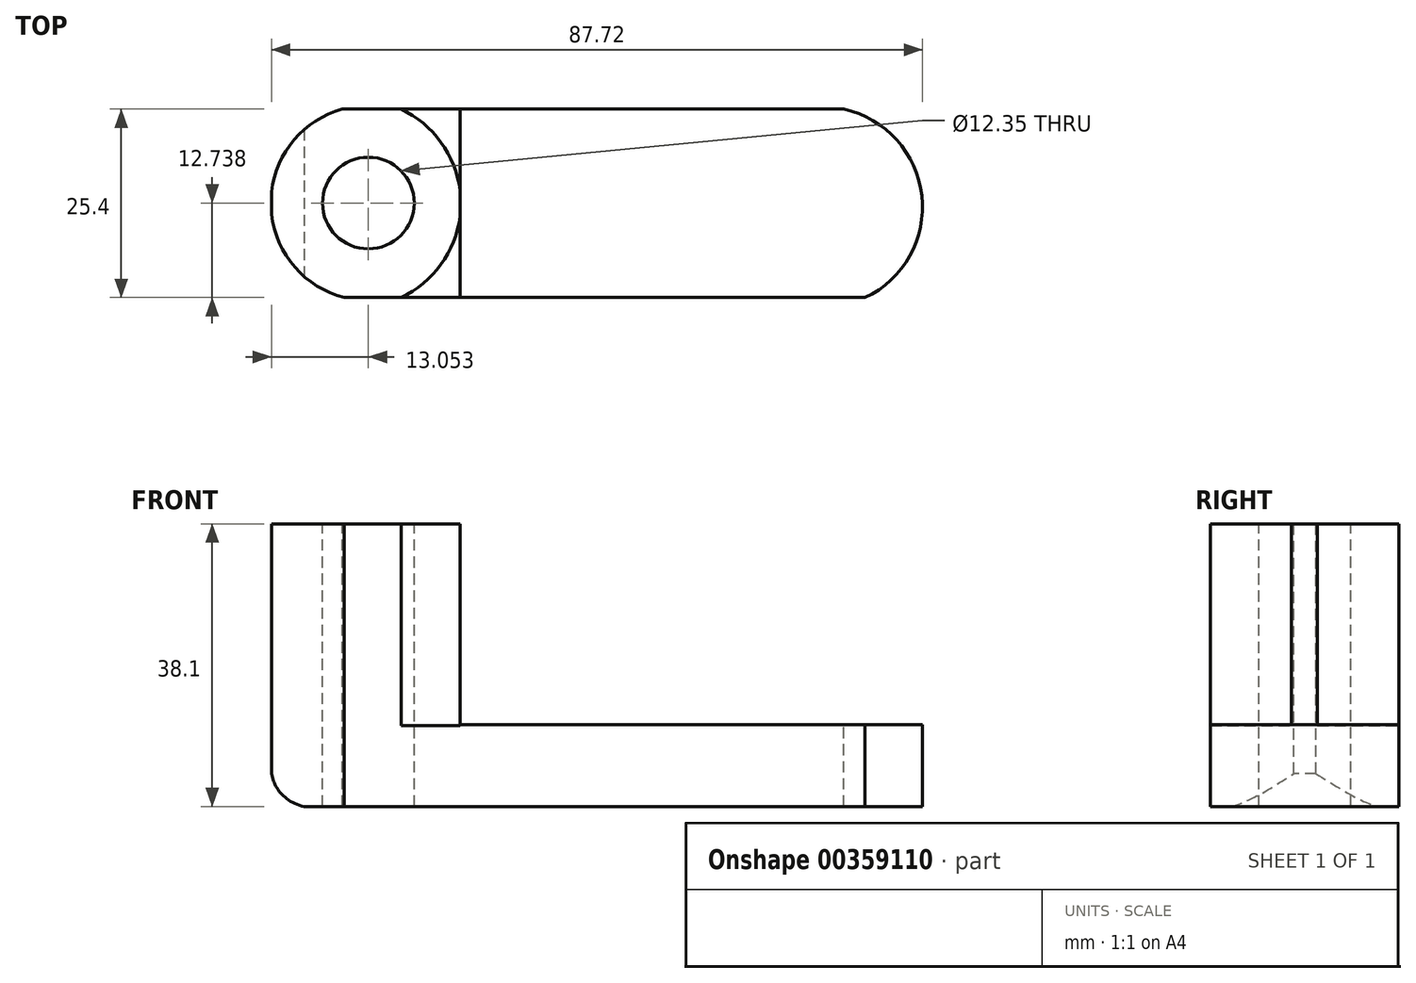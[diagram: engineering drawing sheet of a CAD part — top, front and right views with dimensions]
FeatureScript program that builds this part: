
annotation { "Feature Type Name" : "Feature", "Feature Type Description" : "" }
export const myFeature = defineFeature(function(context is Context, id is Id, definition is map)
    precondition{}
    {
        {
            var Q0;
            Q0=qCreatedBy(makeId("Front.planeOp"),FACE);
            var sketch = newSketch(context, id + "F0", { "sketchPlane" : qUnion([Q0])});
            skLineSegment(sketch, "E0", {"start": v(-42.33, 0) * mm, "end": v(-42.33, 38.1) * mm});
            skLineSegment(sketch, "E1", {"start": v(-42.33, 38.1) * mm, "end": v(-16.93, 38.1) * mm});
            skLineSegment(sketch, "E2", {"start": v(-16.93, 38.1) * mm, "end": v(-16.93, 11) * mm});
            skLineSegment(sketch, "E3", {"start": v(-16.93, 11) * mm, "end": v(46.57, 11) * mm});
            skLineSegment(sketch, "E4", {"start": v(46.57, 11) * mm, "end": v(46.57, 0) * mm});
            skLineSegment(sketch, "E5", {"start": v(46.57, 0) * mm, "end": v(-42.33, 0) * mm});
            skSolve(sketch);
        }
        {
            var Q0;
            Q0=makeQuery(id+"F0.imprint","IMPRINT",FACE,{"disambiguationData":[TD([[makeQuery(id+"F0.imprint","IMPRINT",EDGE,{"derivedFrom":sQuery(id+"F0.wireOp",EDGE,"E0")}),-1.0]])]});
            extrude(context, id + "F1", {"entities" : qUnion([Q0]), "depth" : 25.4 * mm});
        }
        {
            var Q0;
            Q0=makeQuery(id+"F1.opExtrude","CAP_FACE",FACE,{"disambiguationData":[OSD([sQuery(id+"F0.wireOp",EDGE,"E0"),sQuery(id+"F0.wireOp",EDGE,"E1"),sQuery(id+"F0.wireOp",EDGE,"E2"),sQuery(id+"F0.wireOp",EDGE,"E3"),sQuery(id+"F0.wireOp",EDGE,"E4"),sQuery(id+"F0.wireOp",EDGE,"E5")])],"isStart":false});
            var sketch = newSketch(context, id + "F2", { "sketchPlane" : qUnion([Q0])});
            skArc(sketch, "E6", {"start": v(-42.33, 4.42) * mm, "mid": v(-40.05, 0.89) * mm, "end": v(-35.94, 0) * mm});
            skSolve(sketch);
        }
        {
            var Q0;
            {var subQ0=sQuery(id+"F2.wireOp",EDGE,"E6");var subQ1=makeQuery(id+"F1.opExtrude","CAP_EDGE",EDGE,{"disambiguationData":[OSD([sQuery(id+"F0.wireOp",EDGE,"E0")])],"isStart":false});var subQ2=makeQuery(id+"F2.imprint","INTERSECT",VERTEX,{"derivedFrom":[subQ1,subQ0]});Q0=makeQuery(id+"F2.imprint","IMPRINT",FACE,{"disambiguationData":[TD([[makeQuery(id+"F2.imprint","IMPRINT",EDGE,{"disambiguationData":[TD([[subQ2,-1.0]])],"derivedFrom":subQ0}),-1.0]])]});}
            extrude(context, id + "F3", {"entities" : qUnion([Q0]), "operationType" : NewBodyOperationType.REMOVE, "oppositeDirection" : true, "depth" : 25.4 * mm});
        }
        {
            var Q0;
            Q0=makeQuery(id+"F1.opExtrude","SWEPT_FACE",FACE,{"disambiguationData":[OSD([sQuery(id+"F0.wireOp",EDGE,"E3")])]});
            var sketch = newSketch(context, id + "F4", { "sketchPlane" : qUnion([Q0])});
            skArc(sketch, "E7", {"start": v(37.65, -25.4) * mm, "mid": v(45.3, -11.68) * mm, "end": v(34.8, 0) * mm});
            skSolve(sketch);
        }
        {
            var Q0;
            {var subQ0=sQuery(id+"F4.wireOp",EDGE,"E7");Q0=makeQuery(id+"F4.imprint","IMPRINT",FACE,{"disambiguationData":[TD([[makeQuery(id+"F4.imprint","IMPRINT",EDGE,{"derivedFrom":subQ0}),-1.0]])]});}
            extrude(context, id + "F5", {"entities" : qUnion([Q0]), "operationType" : NewBodyOperationType.REMOVE, "oppositeDirection" : true, "depth" : 25.4 * mm});
        }
        {
            var Q0;
            Q0=makeQuery(id+"F1.opExtrude","SWEPT_FACE",FACE,{"disambiguationData":[OSD([sQuery(id+"F0.wireOp",EDGE,"E1")])]});
            var sketch = newSketch(context, id + "F6", { "sketchPlane" : qUnion([Q0])});
            skCircle(sketch, "E8", {"center": v(-31.1, -11.27) * mm, "radius": 19.57 * mm});
            skSolve(sketch);
        }
        {
            var Q0;
            {var subQ0=sQuery(id+"F0.wireOp",EDGE,"E1");var subQ1=makeQuery(id+"F1.opExtrude","CAP_EDGE",EDGE,{"disambiguationData":[OSD([subQ0])],"isStart":true});Q0=makeQuery(id+"F6.imprint","IMPRINT",FACE,{"disambiguationData":[TD([[makeQuery(id+"F6.imprint","IMPRINT",EDGE,{"derivedFrom":subQ1}),1.0]])]});}
            extrude(context, id + "F7", {"entities" : qUnion([Q0]), "operationType" : NewBodyOperationType.REMOVE, "oppositeDirection" : true, "depth" : 25.4 * mm});
        }
        {
            var Q0;
            Q0=makeQuery(id+"F1.opExtrude","SWEPT_FACE",FACE,{"disambiguationData":[OSD([sQuery(id+"F0.wireOp",EDGE,"E1")])]});
            var sketch = newSketch(context, id + "F8", { "sketchPlane" : qUnion([Q0])});
            skArc(sketch, "E9", {"start": v(-32.8, 0) * mm, "mid": v(-42.42, -12.8) * mm, "end": v(-32.52, -25.4) * mm});
            skSolve(sketch);
        }
        {
            var Q0;
            {var subQ0=sQuery(id+"F8.wireOp",EDGE,"E9");var subQ1=sQuery(id+"F0.wireOp",EDGE,"E1");var subQ2=makeQuery(id+"F1.opExtrude","CAP_EDGE",EDGE,{"disambiguationData":[OSD([subQ1])],"isStart":true});var subQ3=makeQuery(id+"F8.imprint","INTERSECT",VERTEX,{"derivedFrom":[subQ2,subQ0]});Q0=makeQuery(id+"F8.imprint","IMPRINT",FACE,{"disambiguationData":[TD([[makeQuery(id+"F8.imprint","IMPRINT",EDGE,{"disambiguationData":[TD([[subQ3,-1.0]])],"derivedFrom":subQ0}),-1.0]])]});}
            var Q1;
            {var subQ0=sQuery(id+"F8.wireOp",EDGE,"E9");var subQ1=sQuery(id+"F0.wireOp",EDGE,"E1");var subQ2=makeQuery(id+"F1.opExtrude","CAP_EDGE",EDGE,{"disambiguationData":[OSD([subQ1])],"isStart":false});var subQ3=makeQuery(id+"F8.imprint","INTERSECT",VERTEX,{"derivedFrom":[subQ2,subQ0]});Q1=makeQuery(id+"F8.imprint","IMPRINT",FACE,{"disambiguationData":[TD([[makeQuery(id+"F8.imprint","IMPRINT",EDGE,{"disambiguationData":[TD([[subQ3,1.0]])],"derivedFrom":subQ0}),-1.0]])]});}
            extrude(context, id + "F9", {"entities" : qUnion([Q0, Q1]), "operationType" : NewBodyOperationType.REMOVE, "oppositeDirection" : true, "depth" : 50.8 * mm});
        }
        {
            var Q0;
            Q0=makeQuery(id+"F1.opExtrude","SWEPT_FACE",FACE,{"disambiguationData":[OSD([sQuery(id+"F0.wireOp",EDGE,"E1")])]});
            var sketch = newSketch(context, id + "F10", { "sketchPlane" : qUnion([Q0])});
            skArc(sketch, "E10", {"start": v(-24.87, -25.4) * mm, "mid": v(-16.82, -12.7) * mm, "end": v(-24.87, 0) * mm});
            skPoint(sketch, "E10.startSnap0", {"position": v(-24.87, 0) * mm});
            skSolve(sketch);
        }
        {
            var Q0;
            {var subQ0=sQuery(id+"F10.wireOp",EDGE,"E10");var subQ1=sQuery(id+"F0.wireOp",EDGE,"E1");var subQ2=makeQuery(id+"F1.opExtrude","CAP_EDGE",EDGE,{"disambiguationData":[OSD([subQ1])],"isStart":true});var subQ3=makeQuery(id+"F10.imprint","INTERSECT",VERTEX,{"derivedFrom":[subQ2,subQ0]});Q0=makeQuery(id+"F10.imprint","IMPRINT",FACE,{"disambiguationData":[TD([[makeQuery(id+"F10.imprint","IMPRINT",EDGE,{"disambiguationData":[TD([[subQ3,1.0]])],"derivedFrom":subQ0}),-1.0]])]});}
            var Q1;
            {var subQ0=sQuery(id+"F10.wireOp",EDGE,"E10");var subQ1=sQuery(id+"F0.wireOp",EDGE,"E1");var subQ2=makeQuery(id+"F1.opExtrude","CAP_EDGE",EDGE,{"disambiguationData":[OSD([subQ1])],"isStart":false});var subQ3=makeQuery(id+"F10.imprint","INTERSECT",VERTEX,{"derivedFrom":[subQ2,subQ0]});Q1=makeQuery(id+"F10.imprint","IMPRINT",FACE,{"disambiguationData":[TD([[makeQuery(id+"F10.imprint","IMPRINT",EDGE,{"disambiguationData":[TD([[subQ3,-1.0]])],"derivedFrom":subQ0}),-1.0]])]});}
            extrude(context, id + "F11", {"entities" : qUnion([Q0, Q1]), "operationType" : NewBodyOperationType.REMOVE, "oppositeDirection" : true, "depth" : 27.18 * mm});
        }
        {
            var Q0;
            Q0=makeQuery(id+"F1.opExtrude","SWEPT_FACE",FACE,{"disambiguationData":[OSD([sQuery(id+"F0.wireOp",EDGE,"E3")])]});
            var sketch = newSketch(context, id + "F12", { "sketchPlane" : qUnion([Q0])});
            skCircle(sketch, "E11", {"center": v(0, -5.48) * mm, "radius": 7.53 * mm});
            skPoint(sketch, "E11.centerSnap0", {"position": v(-16.93, -5.48) * mm});
            skCircle(sketch, "E12", {"center": v(20.54, -5.48) * mm, "radius": 7.68 * mm});
            skLineSegment(sketch, "E13", {"start": v(0, 2.05) * mm, "end": v(20.48, 2.2) * mm});
            skLineSegment(sketch, "E14", {"start": v(0, -13) * mm, "end": v(22.06, -13) * mm});
            skSolve(sketch);
        }
        {
            var Q0;
            {var subQ0=sQuery(id+"F12.wireOp",EDGE,"E11");var subQ1=makeQuery(id+"F12.imprint","INTERSECT",VERTEX,{"derivedFrom":[subQ0,sQuery(id+"F12.wireOp",EDGE,"E13")]});Q0=makeQuery(id+"F12.imprint","IMPRINT",FACE,{"disambiguationData":[TD([[makeQuery(id+"F12.imprint","IMPRINT",EDGE,{"disambiguationData":[TD([[subQ1,-1.0]])],"derivedFrom":subQ0}),1.0]])]});}
            var Q1;
            {var subQ0=sQuery(id+"F12.wireOp",EDGE,"E13");Q1=makeQuery(id+"F12.imprint","IMPRINT",FACE,{"disambiguationData":[TD([[makeQuery(id+"F12.imprint","IMPRINT",EDGE,{"derivedFrom":subQ0}),-1.0]])]});}
            var Q2;
            {var subQ0=sQuery(id+"F12.wireOp",EDGE,"E12");var subQ1=makeQuery(id+"F12.imprint","INTERSECT",VERTEX,{"derivedFrom":[subQ0,sQuery(id+"F12.wireOp",EDGE,"E13")]});Q2=makeQuery(id+"F12.imprint","IMPRINT",FACE,{"disambiguationData":[TD([[makeQuery(id+"F12.imprint","IMPRINT",EDGE,{"disambiguationData":[TD([[subQ1,-1.0]])],"derivedFrom":subQ0}),1.0]])]});}
            extrude(context, id + "F13", {"entities" : qUnion([Q0, Q1, Q2]), "operationType" : NewBodyOperationType.REMOVE, "oppositeDirection" : true, "depth" : 25.4 * mm});
        }
        {
            var Q0;
            Q0=makeQuery(id+"F1.opExtrude","SWEPT_FACE",FACE,{"disambiguationData":[OSD([sQuery(id+"F0.wireOp",EDGE,"E1")])]});
            var sketch = newSketch(context, id + "F14", { "sketchPlane" : qUnion([Q0])});
            skCircle(sketch, "E15", {"center": v(-29.28, -12.66) * mm, "radius": 6.18 * mm});
            skSolve(sketch);
        }
        {
            var Q0;
            Q0=makeQuery(id+"F14.imprint","IMPRINT",FACE,{"disambiguationData":[TD([[makeQuery(id+"F14.imprint","IMPRINT",EDGE,{"derivedFrom":sQuery(id+"F14.wireOp",EDGE,"E15")}),1.0]])]});
            extrude(context, id + "F15", {"entities" : qUnion([Q0]), "operationType" : NewBodyOperationType.REMOVE, "oppositeDirection" : true, "depth" : 50.8 * mm});
        }
    });
